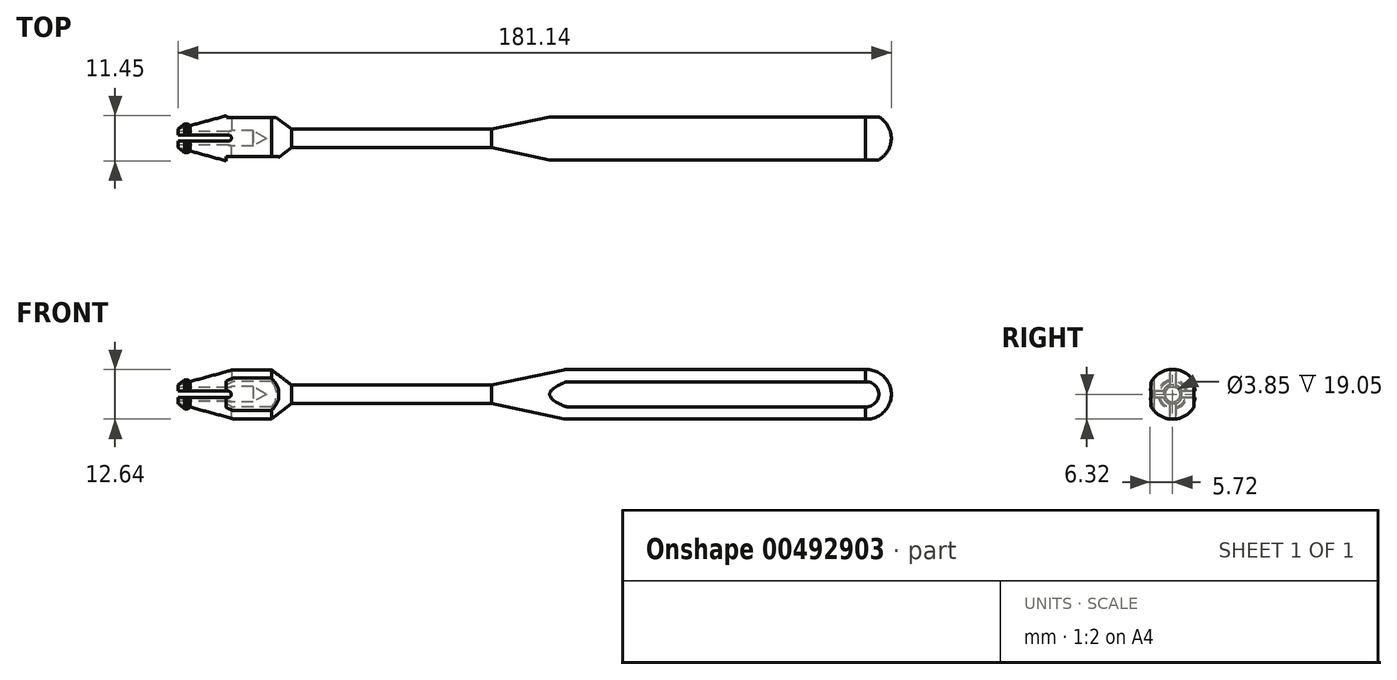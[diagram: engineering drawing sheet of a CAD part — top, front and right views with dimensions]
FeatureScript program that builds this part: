
annotation { "Feature Type Name" : "Feature", "Feature Type Description" : "" }
export const myFeature = defineFeature(function(context is Context, id is Id, definition is map)
    precondition{}
    {
        {
            var Q0;
            Q0=qCreatedBy(makeId("Front.planeOp"),FACE);
            var sketch = newSketch(context, id + "F0", { "sketchPlane" : qUnion([Q0])});
            skLineSegment(sketch, "E0", {"start": v(0, -0.03) * mm, "end": v(0, 0) * mm});
            skLineSegment(sketch, "E1", {"start": v(-152.4, 0) * mm, "end": v(0, 0) * mm});
            skPoint(sketch, "E2.visualSharp", {"position": v(0, 6.35) * mm});
            skArc(sketch, "E2.filletArc", {"start": v(0, -0.03) * mm, "mid": v(-1.92, 4.51) * mm, "end": v(-6.5, 6.32) * mm});
            skLineSegment(sketch, "E3", {"start": v(-6.5, 6.32) * mm, "end": v(-82.22, 6.32) * mm});
            skLineSegment(sketch, "E4", {"start": v(-101.6, 2.39) * mm, "end": v(-83.19, 6.22) * mm});
            skPoint(sketch, "E5.visualSharp", {"position": v(-82.7, 6.32) * mm});
            skArc(sketch, "E5.filletArc", {"start": v(-82.22, 6.32) * mm, "mid": v(-82.7, 6.3) * mm, "end": v(-83.19, 6.22) * mm});
            skLineSegment(sketch, "E6", {"start": v(-101.6, 2.39) * mm, "end": v(-152.4, 2.39) * mm});
            skLineSegment(sketch, "E7", {"start": v(-152.4, 0) * mm, "end": v(-158.75, 0) * mm});
            skLineSegment(sketch, "E8", {"start": v(-158.75, 0) * mm, "end": v(-162.09, 1.93) * mm});
            skLineSegment(sketch, "E9", {"start": v(-162.09, 1.93) * mm, "end": v(-181.14, 1.93) * mm});
            skLineSegment(sketch, "E10", {"start": v(-181.14, 1.93) * mm, "end": v(-181.14, 2.51) * mm});
            skLineSegment(sketch, "E11", {"start": v(-167, 6.23) * mm, "end": v(-157.46, 6.23) * mm});
            skLineSegment(sketch, "E12", {"start": v(-167.52, 6.16) * mm, "end": v(-181.14, 2.51) * mm});
            skLineSegment(sketch, "E13", {"start": v(-157.46, 6.23) * mm, "end": v(-152.4, 2.39) * mm});
            skPoint(sketch, "E14.visualSharp", {"position": v(-167.26, 6.23) * mm});
            skArc(sketch, "E14.filletArc", {"start": v(-167, 6.23) * mm, "mid": v(-167.26, 6.21) * mm, "end": v(-167.52, 6.16) * mm});
            skSolve(sketch);
        }
        {
            var Q0;
            {var subQ0=sQuery(id+"F0.wireOp",EDGE,"E1");Q0=makeQuery(id+"F0.imprint","IMPRINT",FACE,{"disambiguationData":[TD([[makeQuery(id+"F0.imprint","IMPRINT",EDGE,{"derivedFrom":subQ0}),1.0]])]});}
            var Q1;
            Q1=sQuery(id+"F0.wireOp",EDGE,"E1");
            revolve(context, id + "F1", {"entities" : qUnion([Q0]), "axis" : qUnion([Q1]), "revolveType" : RevolveType.FULL});
        }
        {
            var Q0;
            Q0=qCreatedBy(makeId("Top.planeOp"),FACE);
            var sketch = newSketch(context, id + "F2", { "sketchPlane" : qUnion([Q0])});
            skLineSegment(sketch, "E15", {"start": v(-181.14, 2.51) * mm, "end": v(-178.07, 3.34) * mm});
            skLineSegment(sketch, "E16", {"start": v(-179.53, 3.76) * mm, "end": v(-178.8, 3.76) * mm});
            skLineSegment(sketch, "E17", {"start": v(-178.8, 3.76) * mm, "end": v(-178.07, 3.34) * mm});
            skLineSegment(sketch, "E18", {"start": v(-179.53, 3.76) * mm, "end": v(-181.14, 2.51) * mm});
            skSolve(sketch);
        }
        {
            var Q0;
            Q0 = qSketchRegion(id + "F2", true);
            var Q1;
            Q1=makeQuery(id+"F1.opRevolve","SWEPT_FACE",FACE,{"disambiguationData":[OSD([sQuery(id+"F0.wireOp",EDGE,"E12")])]});
            revolve(context, id + "F3", {"entities" : qUnion([Q0]), "axis" : qUnion([Q1]), "revolveType" : RevolveType.FULL});
        }
        {
            var Q0;
            Q0=qCreatedBy(makeId("Top.planeOp"),FACE);
            var sketch = newSketch(context, id + "F4", { "sketchPlane" : qUnion([Q0])});
            skLineSegment(sketch, "E19", {"start": v(-181.14, 0.87) * mm, "end": v(-168.44, 0.87) * mm});
            skLineSegment(sketch, "E20", {"start": v(-181.14, -0.73) * mm, "end": v(-168.44, -0.73) * mm});
            skArc(sketch, "E21", {"start": v(-168.44, 0.87) * mm, "mid": v(-167.64, 0.07) * mm, "end": v(-168.44, -0.73) * mm});
            skLineSegment(sketch, "E22", {"start": v(-181.14, 0.87) * mm, "end": v(-181.17, 0.87) * mm});
            skLineSegment(sketch, "E23", {"start": v(-181.14, -0.73) * mm, "end": v(-181.17, -0.73) * mm});
            skLineSegment(sketch, "E24", {"start": v(-181.17, -0.73) * mm, "end": v(-181.17, 0.87) * mm});
            skSolve(sketch);
        }
        {
            var Q0;
            Q0 = qSketchRegion(id + "F4", true);
            extrude(context, id + "F5", {"entities" : qUnion([Q0]), "operationType" : NewBodyOperationType.REMOVE, "oppositeDirection" : true, "depth" : 25.4 * mm});
        }
        {
            var Q0;
            Q0 = qSketchRegion(id + "F4", true);
            extrude(context, id + "F6", {"entities" : qUnion([Q0]), "operationType" : NewBodyOperationType.REMOVE, "depth" : 25.4 * mm});
        }
        {
            var Q0;
            Q0=qCreatedBy(makeId("Front.planeOp"),FACE);
            var sketch = newSketch(context, id + "F7", { "sketchPlane" : qUnion([Q0])});
            skLineSegment(sketch, "E25", {"start": v(-181.14, 0) * mm, "end": v(-181.14, 0.79) * mm});
            skLineSegment(sketch, "E26", {"start": v(-181.14, 0) * mm, "end": v(-181.14, -0.79) * mm});
            skLineSegment(sketch, "E27", {"start": v(-181.14, 0.79) * mm, "end": v(-168.44, 0.79) * mm});
            skLineSegment(sketch, "E28", {"start": v(-181.14, -0.79) * mm, "end": v(-168.44, -0.79) * mm});
            skArc(sketch, "E29", {"start": v(-168.44, 0.79) * mm, "mid": v(-167.65, 0) * mm, "end": v(-168.44, -0.79) * mm});
            skSolve(sketch);
        }
        {
            var Q0;
            Q0 = qSketchRegion(id + "F7", true);
            extrude(context, id + "F8", {"entities" : qUnion([Q0]), "operationType" : NewBodyOperationType.REMOVE, "oppositeDirection" : true, "depth" : 25.4 * mm});
        }
        {
            var Q0;
            Q0 = qSketchRegion(id + "F7", true);
            extrude(context, id + "F9", {"entities" : qUnion([Q0]), "operationType" : NewBodyOperationType.REMOVE, "depth" : 25.4 * mm});
        }
        {
            var Q0;
            Q0=qCreatedBy(makeId("Top.planeOp"),FACE);
            var sketch = newSketch(context, id + "F10", { "sketchPlane" : qUnion([Q0])});
            skLineSegment(sketch, "E30", {"start": v(0, 5.46) * mm, "end": v(-89.53, 5.46) * mm});
            skLineSegment(sketch, "E31", {"start": v(-89.53, 7.36) * mm, "end": v(0, 7.36) * mm});
            skLineSegment(sketch, "E32", {"start": v(-155.58, 7.36) * mm, "end": v(-155.58, 5.33) * mm});
            skLineSegment(sketch, "E33", {"start": v(-155.58, 7.36) * mm, "end": v(-168.93, 7.36) * mm});
            skLineSegment(sketch, "E34", {"start": v(-155.58, 5.33) * mm, "end": v(-168.93, 5.33) * mm});
            skLineSegment(sketch, "E35", {"start": v(-168.93, 5.33) * mm, "end": v(-168.93, 7.36) * mm});
            skLineSegment(sketch, "E36", {"start": v(-89.53, 5.46) * mm, "end": v(-89.53, 7.36) * mm});
            skLineSegment(sketch, "E37", {"start": v(0, 7.36) * mm, "end": v(0, 5.46) * mm});
            skSolve(sketch);
        }
        {
            var Q0;
            Q0 = qSketchRegion(id + "F10", true);
            extrude(context, id + "F11", {"entities" : qUnion([Q0]), "operationType" : NewBodyOperationType.REMOVE, "endBound" : BoundingType.SYMMETRIC, "depth" : 25.4 * mm});
        }
        {
            var Q0;
            Q0=qCreatedBy(makeId("Top.planeOp"),FACE);
            var sketch = newSketch(context, id + "F12", { "sketchPlane" : qUnion([Q0])});
            skLineSegment(sketch, "E38", {"start": v(0, -5.47) * mm, "end": v(0, -6.71) * mm});
            skLineSegment(sketch, "E39", {"start": v(0, -6.71) * mm, "end": v(-89.56, -6.71) * mm});
            skLineSegment(sketch, "E40", {"start": v(0, -5.47) * mm, "end": v(-89.56, -5.47) * mm});
            skLineSegment(sketch, "E41", {"start": v(-89.56, -5.47) * mm, "end": v(-89.56, -6.71) * mm});
            skLineSegment(sketch, "E42", {"start": v(-155.63, -6.71) * mm, "end": v(-155.63, -4.67) * mm});
            skLineSegment(sketch, "E43", {"start": v(-155.63, -4.67) * mm, "end": v(-168.96, -4.67) * mm});
            skLineSegment(sketch, "E44", {"start": v(-168.96, -4.67) * mm, "end": v(-168.96, -6.71) * mm});
            skLineSegment(sketch, "E45", {"start": v(-168.96, -6.71) * mm, "end": v(-155.63, -6.71) * mm});
            skSolve(sketch);
        }
        {
            var Q0;
            Q0 = qSketchRegion(id + "F12", true);
            extrude(context, id + "F13", {"entities" : qUnion([Q0]), "operationType" : NewBodyOperationType.REMOVE, "endBound" : BoundingType.SYMMETRIC, "oppositeDirection" : true, "depth" : 25.4 * mm});
        }
    });
